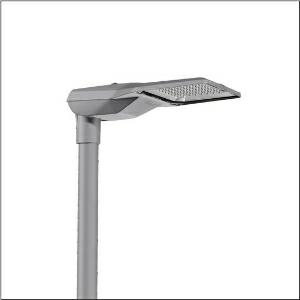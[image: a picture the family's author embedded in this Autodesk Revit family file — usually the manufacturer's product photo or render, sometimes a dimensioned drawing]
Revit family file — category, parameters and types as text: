
# Revit family: streetlight_sl_21_midi___st1_0a_5xe3d43s08nb_04c9
name_source: partatom
category: Lighting Fixtures
units: mm (PartAtom-declared; Revit-internal decimal feet)

## family parameters
Cut with Voids When Loaded = No
Host = Face
Light Source = No
Part Type = Normal
Room Calculation Point = No
Round Connector Dimension = Use Diameter
Shared = No

## types (1)
- --- (1 x LED, 23710 lm, 151.2 W, 4000K)
    Apparent Load = 151 VA
    CIE Flux Codes = 40 73 97 100 100
    Color Rendering = 70
    Color Temperature = 4000K
    Default Elevation = 1800 mm
    Description = Streetlight SL 21 midi, mast luminaire, primary light control with lens, of PMMA, primary optical cover: cover, of toughened safety glass, transparent, light distribution: ST1.0a, light emission: direct distribution, primary light characteristic: asymmetric, installation type: side-entry, post-top, LED, High Power LED, rated luminous flux: 23.710lm, luminous efficacy: 157lm/W, light colour: 740, colour temperature: 4000K, control gear: D4i, control: overheat protection, constant luminous flux control, time-dependent luminous flux control, flexible luminous flux parameterisation, pre-setting: logarithmic dimming characteristic, mains connection: 230..240V, AC, 50/60Hz, start of lifetime: 151W, end of service life: 157W, reduction: 70W, luminaire housing, of diecast aluminium, powder-coated, Siteco® metallic grey (DB 702S), corrosivity category C5 mid according to DIN EN ISO 12944, please order mast flange separately, inclination adjustable: 0°, 5°, 10°, 15°, sealing non-destructively replaceable, multi-level sealing system, length: 644mm, width: 335mm, height: 110mm, mast flange for spigot size: 42mm (side-entry): 5XC10008XM4, 60/48mm (side-entry/post-top): 5XC10108XM2, 76/60mm (side-entry/post-top): 5XC10108XM1, mounting height: 4..8m, Smart Interface above, protection rating (complete): IP66, insulation class (complete): insulation class II (safety insulation), certification: CE, ENEC, ENEC+, VDE, impact resistance: IK10, permissible operating ambient temperature for outdoor applications: -40..+50°C, standard-compliant lighting for roads and squares, packaging unit: 1 piece

Light Distribution: ST1.0a
    Height = 111 mm
    Lamp = 1 x LED
    Lamp Light Flux = 23710 lm
    Lamp Power = 151.2 W
    Lamp count = 1
    Length = 644 mm
    Luminous efficacy = 157 lm/W
    Manufacturer = Siteco
    ModVariant = No
    Model = 5XE3D43S08NB
    Number of Poles = 1
    OnlyDefault = Yes
    Power Factor = 1
    Product Name = Streetlight SL 21 midi | ST1.0a
    Product group = mast luminaire | pylon top
    ProductGroupID = 6100
    Protection Class = Protection class II
    Protection Degree = IP 66
    RLX_Detail_Level = 1
    RLX_Emergency_Light_Flux = 0 lm
    RLX_Emergency_Type = 0
    RLX_Emergency_Type_DB = No
    RlxData = <blob elided: 26965 chars, md5=83a5c82c>
    Socket = socket
    Standby Power = 0 W
    System Light Flux = 23710 lm
    System Power = 151 W
    Type Comments = factory setting: luminous flux: 100 % | dim-lin: 254 | 802 mA
    Type Image = l_1004302.jpg
    URL = http://relux.com
    VarID = @adj_170576
    Voltage = 0 V
    Weight = 0.00 kg
    Width = 336 mm

## geometry (parser evidence)
native form markers: Blend x4, Sweep x9
no freeform markers — native parametric forms only
